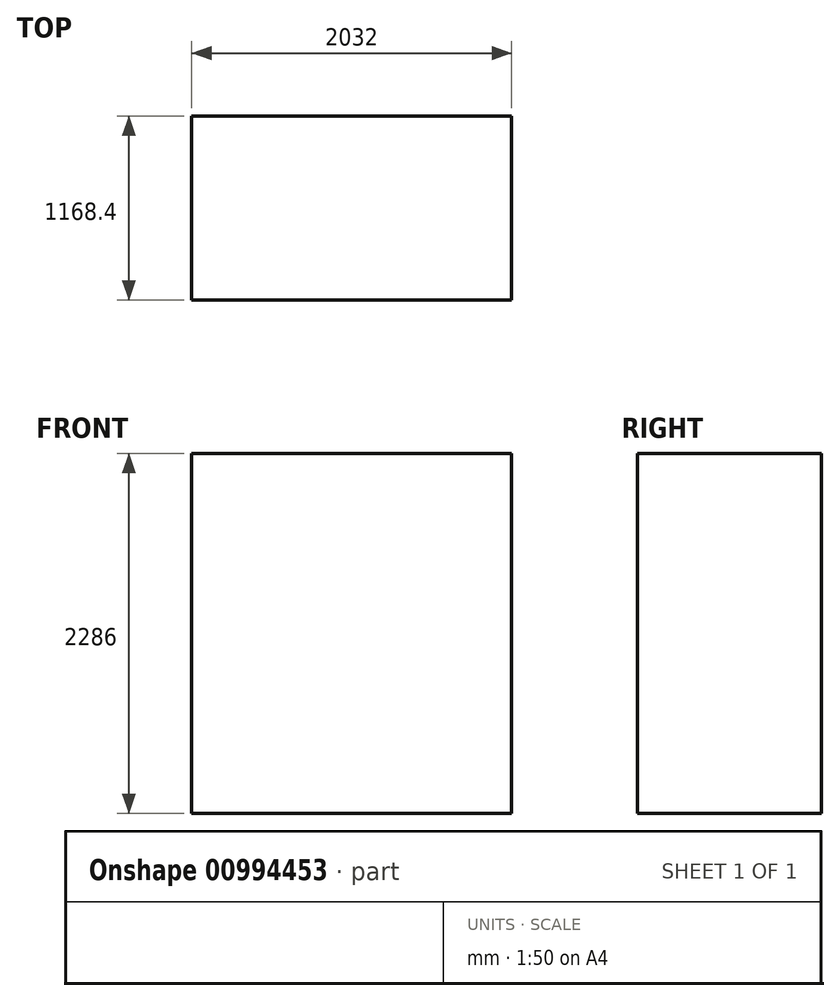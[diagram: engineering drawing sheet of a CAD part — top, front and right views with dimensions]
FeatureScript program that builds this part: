
annotation { "Feature Type Name" : "Feature", "Feature Type Description" : "" }
export const myFeature = defineFeature(function(context is Context, id is Id, definition is map)
    precondition{}
    {
        {
            var Q0;
            Q0=qCreatedBy(makeId("Top.planeOp"),FACE);
            var sketch = newSketch(context, id + "F0", { "sketchPlane" : qUnion([Q0])});
            skLineSegment(sketch, "E0.bottom", {"start": v(0, 0) * mm, "end": v(2032, 0) * mm});
            skLineSegment(sketch, "E0.top", {"start": v(0, 1168.4) * mm, "end": v(2032, 1168.4) * mm});
            skLineSegment(sketch, "E0.left", {"start": v(0, 0) * mm, "end": v(0, 1168.4) * mm});
            skLineSegment(sketch, "E0.right", {"start": v(2032, 0) * mm, "end": v(2032, 1168.4) * mm});
            skSolve(sketch);
        }
        {
            var Q0;
            Q0 = qSketchRegion(id + "F0", true);
            extrude(context, id + "F1", {"entities" : qUnion([Q0]), "depth" : 2286 * mm, "offsetDistance" : 25.4 * mm});
        }
    });
